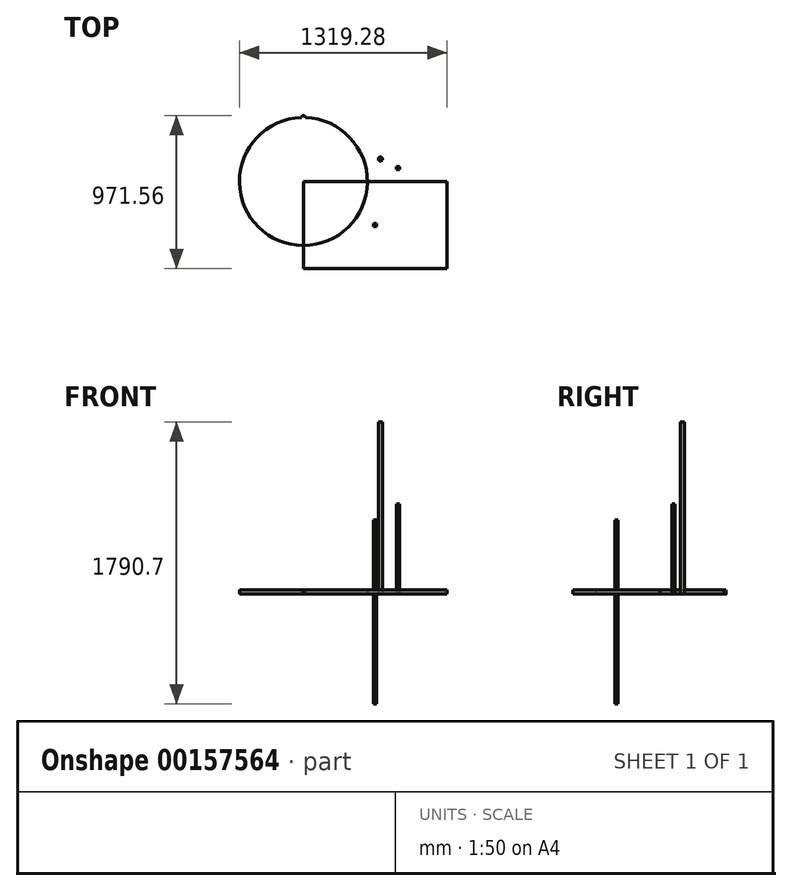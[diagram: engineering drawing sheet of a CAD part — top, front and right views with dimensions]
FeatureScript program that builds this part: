
annotation { "Feature Type Name" : "Feature", "Feature Type Description" : "" }
export const myFeature = defineFeature(function(context is Context, id is Id, definition is map)
    precondition{}
    {
        {
            var Q0;
            Q0=qCreatedBy(makeId("Top.planeOp"),FACE);
            var sketch = newSketch(context, id + "F0", { "sketchPlane" : qUnion([Q0])});
            skLineSegment(sketch, "E0.bottom", {"start": v(456.44, 276.23) * mm, "end": v(-456.44, 276.23) * mm});
            skLineSegment(sketch, "E0.top", {"start": v(456.44, -276.23) * mm, "end": v(-456.44, -276.23) * mm});
            skLineSegment(sketch, "E0.left", {"start": v(456.44, 276.22) * mm, "end": v(456.44, -276.23) * mm});
            skLineSegment(sketch, "E0.right", {"start": v(-456.44, 276.23) * mm, "end": v(-456.44, -276.23) * mm});
            skPoint(sketch, "E0.middle", {"position": v(0, 0) * mm});
            skSolve(sketch);
        }
        {
            var Q0;
            Q0=makeQuery(id+"F0.imprint","IMPRINT",FACE,{"disambiguationData":[TD([[makeQuery(id+"F0.imprint","IMPRINT",EDGE,{"derivedFrom":sQuery(id+"F0.wireOp",EDGE,"E0.bottom")}),1.0]])]});
            var sketch = newSketch(context, id + "F1", { "sketchPlane" : qUnion([Q0])});
            skArc(sketch, "E1", {"start": v(-469.14, 682.43) * mm, "mid": v(-456.44, -130.18) * mm, "end": v(-443.74, 682.43) * mm});
            skArc(sketch, "E2", {"start": v(-443.74, 682.43) * mm, "mid": v(-456.44, 695.33) * mm, "end": v(-469.14, 682.43) * mm});
            skSolve(sketch);
        }
        {
            var Q0;
            Q0=qCreatedBy(makeId("Top.planeOp"),FACE);
            var sketch = newSketch(context, id + "F2", { "sketchPlane" : qUnion([Q0])});
            skCircle(sketch, "E3", {"center": v(32.2, 419.15) * mm, "radius": 12.7 * mm});
            skSolve(sketch);
        }
        {
            var Q0;
            Q0=qCreatedBy(makeId("Top.planeOp"),FACE);
            var sketch = newSketch(context, id + "F3", { "sketchPlane" : qUnion([Q0])});
            skLineSegment(sketch, "E4.bottom", {"start": v(153.12, 371.2) * mm, "end": v(134.07, 371.2) * mm});
            skLineSegment(sketch, "E4.top", {"start": v(153.12, 352.16) * mm, "end": v(134.07, 352.16) * mm});
            skLineSegment(sketch, "E4.left", {"start": v(153.12, 371.2) * mm, "end": v(153.12, 352.16) * mm});
            skLineSegment(sketch, "E4.right", {"start": v(134.07, 371.2) * mm, "end": v(134.07, 352.16) * mm});
            skPoint(sketch, "E4.middle", {"position": v(143.6, 361.68) * mm});
            skSolve(sketch);
        }
        {
            var Q0;
            Q0=makeQuery(id+"F0.imprint","IMPRINT",FACE,{"disambiguationData":[TD([[makeQuery(id+"F0.imprint","IMPRINT",EDGE,{"derivedFrom":sQuery(id+"F0.wireOp",EDGE,"E0.bottom")}),1.0]])]});
            extrude(context, id + "F4", {"entities" : qUnion([Q0]), "depth" : 25.4 * mm});
        }
        {
            var Q0;
            {var subQ0=sQuery(id+"F1.wireOp",EDGE,"E2");Q0=makeQuery(id+"F1.imprint","IMPRINT",FACE,{"disambiguationData":[TD([[makeQuery(id+"F1.imprint","IMPRINT",EDGE,{"derivedFrom":subQ0}),1.0]])]});}
            var Q1;
            {var subQ0=sQuery(id+"F1.wireOp",EDGE,"E1");var subQ1=makeQuery(id+"F0.imprint","IMPRINT",EDGE,{"derivedFrom":sQuery(id+"F0.wireOp",EDGE,"E0.right")});var subQ2=makeQuery(id+"F1.imprint","INTERSECT",VERTEX,{"derivedFrom":[subQ1,subQ0]});Q1=makeQuery(id+"F1.imprint","IMPRINT",FACE,{"disambiguationData":[TD([[makeQuery(id+"F1.imprint","IMPRINT",EDGE,{"disambiguationData":[TD([[subQ2,-1.0]])],"derivedFrom":subQ0}),1.0]])]});}
            extrude(context, id + "F5", {"entities" : qUnion([Q0, Q1]), "depth" : 25.4 * mm});
        }
        {
            var Q0;
            Q0=makeQuery(id+"F2.imprint","IMPRINT",FACE,{"disambiguationData":[TD([[makeQuery(id+"F2.imprint","IMPRINT",EDGE,{"derivedFrom":sQuery(id+"F2.wireOp",EDGE,"E3")}),1.0]])]});
            extrude(context, id + "F6", {"entities" : qUnion([Q0]), "depth" : 1092.2 * mm});
        }
        {
            var Q0;
            Q0=makeQuery(id+"F3.imprint","IMPRINT",FACE,{"disambiguationData":[TD([[makeQuery(id+"F3.imprint","IMPRINT",EDGE,{"derivedFrom":sQuery(id+"F3.wireOp",EDGE,"E4.bottom")}),1.0]])]});
            extrude(context, id + "F7", {"entities" : qUnion([Q0]), "depth" : 571.5 * mm});
        }
        {
            var Q0;
            Q0=makeQuery(id+"F4.opExtrude","CAP_FACE",FACE,{"disambiguationData":[OSD([sQuery(id+"F0.wireOp",EDGE,"E0.bottom"),sQuery(id+"F0.wireOp",EDGE,"E0.top"),sQuery(id+"F0.wireOp",EDGE,"E0.left"),sQuery(id+"F0.wireOp",EDGE,"E0.right")])],"isStart":false});
            var sketch = newSketch(context, id + "F8", { "sketchPlane" : qUnion([Q0])});
            skLineSegment(sketch, "E5.bottom", {"start": v(9.52, 9.52) * mm, "end": v(-9.53, 9.52) * mm});
            skLineSegment(sketch, "E5.top", {"start": v(9.52, -9.53) * mm, "end": v(-9.53, -9.53) * mm});
            skLineSegment(sketch, "E5.left", {"start": v(9.52, 9.52) * mm, "end": v(9.52, -9.53) * mm});
            skLineSegment(sketch, "E5.right", {"start": v(-9.53, 9.52) * mm, "end": v(-9.53, -9.53) * mm});
            skPoint(sketch, "E5.middle", {"position": v(0, 0) * mm});
            skSolve(sketch);
        }
        {
            var Q0;
            Q0=makeQuery(id+"F8.imprint","IMPRINT",FACE,{"disambiguationData":[TD([[makeQuery(id+"F8.imprint","IMPRINT",EDGE,{"derivedFrom":sQuery(id+"F8.wireOp",EDGE,"E5.bottom")}),1.0]])]});
            extrude(context, id + "F9", {"entities" : qUnion([Q0]), "depth" : 444.5 * mm});
        }
        {
            var Q0;
            Q0=makeQuery(id+"F4.opExtrude","CAP_FACE",FACE,{"disambiguationData":[OSD([sQuery(id+"F0.wireOp",EDGE,"E0.bottom"),sQuery(id+"F0.wireOp",EDGE,"E0.top"),sQuery(id+"F0.wireOp",EDGE,"E0.left"),sQuery(id+"F0.wireOp",EDGE,"E0.right")])],"isStart":true});
            var sketch = newSketch(context, id + "F10", { "sketchPlane" : qUnion([Q0])});
            skLineSegment(sketch, "E6.bottom", {"start": v(9.52, 9.53) * mm, "end": v(-9.53, 9.53) * mm});
            skLineSegment(sketch, "E6.top", {"start": v(9.52, -9.52) * mm, "end": v(-9.53, -9.52) * mm});
            skLineSegment(sketch, "E6.left", {"start": v(9.52, 9.53) * mm, "end": v(9.52, -9.52) * mm});
            skLineSegment(sketch, "E6.right", {"start": v(-9.53, 9.53) * mm, "end": v(-9.53, -9.52) * mm});
            skPoint(sketch, "E6.middle", {"position": v(0, 0) * mm});
            skSolve(sketch);
        }
        {
            var Q0;
            Q0=makeQuery(id+"F10.imprint","IMPRINT",FACE,{"disambiguationData":[TD([[makeQuery(id+"F10.imprint","IMPRINT",EDGE,{"derivedFrom":sQuery(id+"F10.wireOp",EDGE,"E6.bottom")}),1.0]])]});
            extrude(context, id + "F11", {"entities" : qUnion([Q0]), "depth" : 698.5 * mm});
        }
    });
